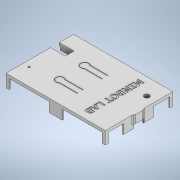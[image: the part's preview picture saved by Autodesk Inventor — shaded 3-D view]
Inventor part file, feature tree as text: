
AUTODESK INVENTOR PART (.ipt)
format: ipt  version: 2020 (Build 240168000, 168)  size: 761,344 bytes
history: native  units: mm
features: extrude x19, sketch x18, projected_geometry x7, fillet x5
ambient origin geometry x8: Origin, YZ Plane, XZ Plane, XY Plane, X Axis, Y Axis, Z Axis, Center Point
bodies: Solid1 (feature_tree)
feature tree (49):
  sketch  "Sketch1"  dims[d0=96.9mm d1=65.9mm]
  extrude  "Extrusion1"  Depth=65.9mm
  extrude  "Extrusion2"  Depth=1.0mm
  sketch  "Sketch3"  dims[d5=3.0mm d6=3.0mm]
  extrude  "Extrusion3"  Depth=3.0mm
  extrude  "Extrusion4"  Depth=12.3mm TaperAngle=0.0deg
  extrude  "Extrusion5"  Depth=8.5mm
  extrude  "Extrusion6"  Depth=12.3mm TaperAngle=0.0deg
  sketch  "Sketch9"  dims[d20=7.0mm d22=0.5mm d24=3.0mm]
  extrude  "Extrusion7"  Depth=31.8mm
  extrude  "Extrusion8"  Depth=0.5mm
  fillet  "Fillet1"  Radius=3.0mm
  extrude  "Extrusion9"  Depth=20.0mm
  extrude  "Extrusion10"  Depth=0.5mm
  fillet  "Fillet2"  Radius=12.3mm
  extrude  "Extrusion11"  Depth=0.5mm
  extrude  "Extrusion12"  Depth=16.5mm
  fillet  "Fillet3"  Radius=11.0mm
  extrude  "Extrusion13"  Depth=1.0mm
  fillet  "Fillet4"  Radius=1.0mm
  extrude  "Extrusion14"  Depth=1.0mm
  extrude  "Extrusion15"  Depth=11.0mm TaperAngle=0.0deg
  extrude  "Extrusion16"  Depth=27.73mm
  extrude  "Extrusion17"  Depth=8.8mm
  extrude  "Extrusion18"  Depth=0.4mm
  fillet  "Fillet5"  Radius=10.0mm
  extrude  "Extrusion19"  Depth=0.4mm TaperAngle=0.0deg
  sketch  "Sketch2"  dims[d2=1.0mm d3=0.0mm d4=1.0mm]
  projected_geometry  "Projected Loop1"
  sketch  "Sketch4"  dims[d7=20.0mm d9=360.0deg d11=12.3mm d12=0.0mm]
  projected_geometry  "Projected Loop2"
  sketch  "Sketch5"  dims[d13=14.0mm d14=8.5mm]
  sketch  "Sketch7"  dims[d15=14.5mm d16=12.3mm d17=0.0mm]
  sketch  "Sketch8"  dims[d18=21.0mm d19=31.8mm]
  sketch  "Sketch10"  dims[d25=3.0mm d26=20.0mm]
  sketch  "Sketch11"  dims[d27=0.5mm d28=0.5mm d29=12.3mm d30=0.0mm]
  projected_geometry  "Projected Loop3"
  sketch  "Sketch12"  dims[d31=7.0mm d32=0.5mm d33=3.0mm d34=3.0mm d35=20.0mm d36=0.5mm d37=0.5mm d38=24.2mm d39=0.5mm]
  projected_geometry  "Projected Loop4"
  sketch  "Sketch13"  dims[d40=6.0mm d41=16.5mm d42=11.0mm d43=0.0mm]
  sketch  "Sketch14"  dims[d44=4.0mm d45=11.4mm d46=1.0mm]
  sketch  "Sketch15"  dims[d47=5.0mm d48=1.0mm]
  projected_geometry  "Projected Loop5"
  sketch  "Sketch16"  dims[d49=13.0mm d50=11.0mm d51=0.0mm]
  projected_geometry  "Projected Loop6"
  sketch  "Sketch17"  dims[d52=9.5mm d53=27.73mm]
  projected_geometry  "Projected Loop7"
  sketch  "Sketch18"  dims[d55=1.1mm d56=8.8mm]
  sketch  "Sketch19"  dims[d57=1.0mm d58=10.0mm d59=10.0mm d60=7.9mm d61=0.0mm d62=7.9mm d63=0.0mm d64=2.0mm d65=5.0mm d66=16.5mm d67=8.9mm d68=0.5mm d69=10.0mm d70=0.0mm d71=10.0mm d72=0.0mm d73=2.0mm d74=1.8mm d75=10.0mm d76=0.0mm d77=15.0mm d78=5.0mm d79=33.0mm d80=10.0mm d81=0.0mm d82=2.0mm d83=5.0mm d84=5.0mm d85=1.9mm d86=0.0mm d87=1.0mm d88=1.0mm d89=1.9mm d90=0.0mm d91=1.9mm d92=0.0mm d93=1.0mm d94=1.0mm d95=1.0mm d96=5.0mm d97=0.0mm d98=1.0mm d99=19.0mm d100=1.0mm d101=5.0mm d102=0.0mm d103=14.5mm d104=5.0mm d105=19.5mm d106=5.0mm d107=0.0mm d108=1.5mm d109=0.4mm d110=0.0mm]
